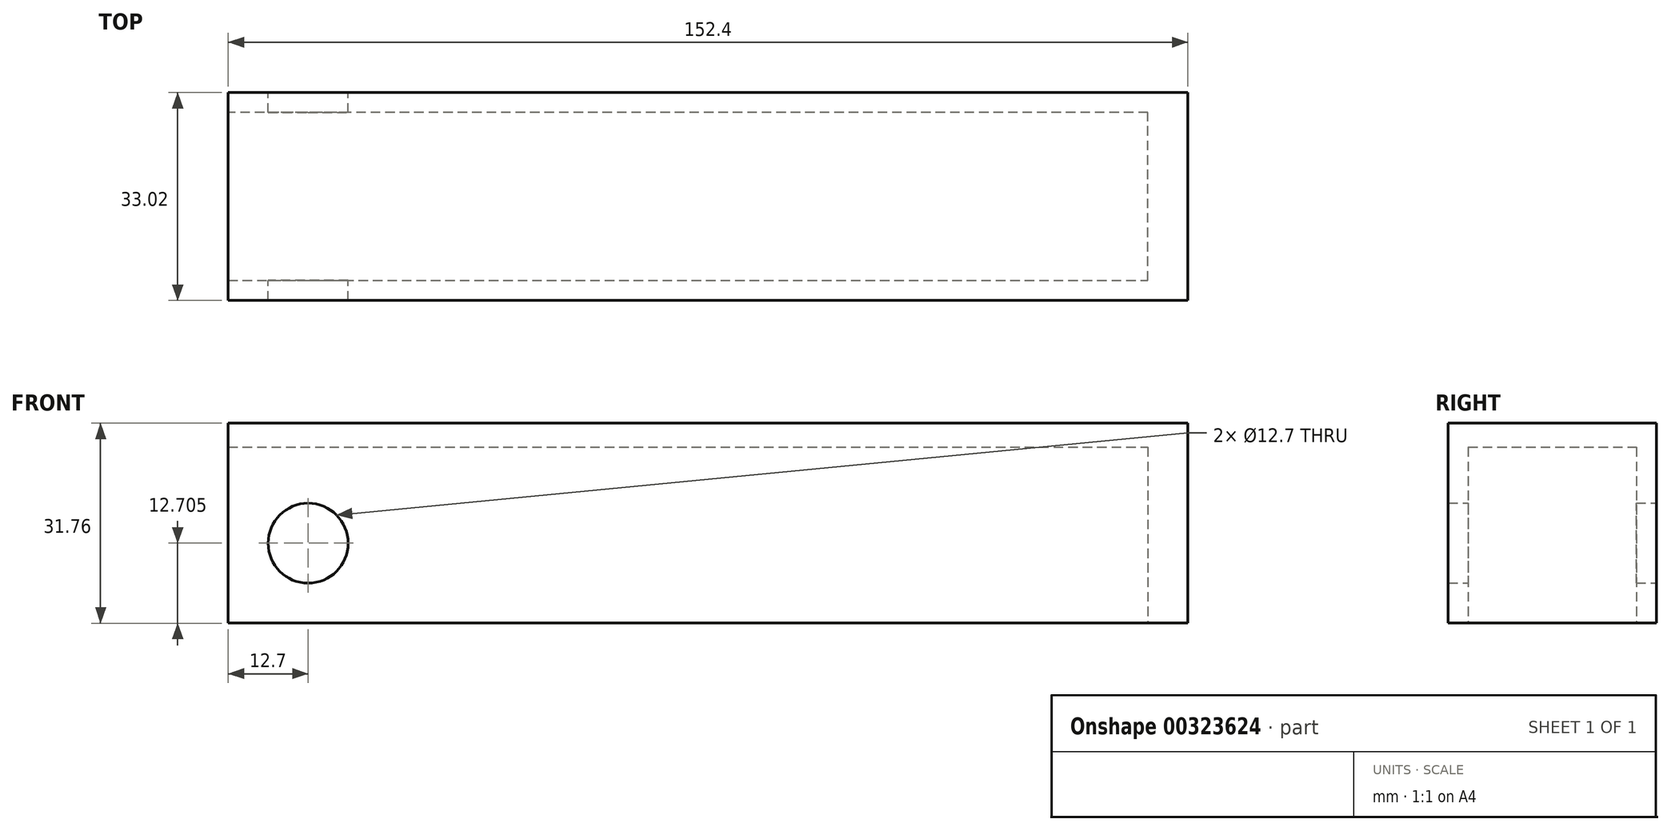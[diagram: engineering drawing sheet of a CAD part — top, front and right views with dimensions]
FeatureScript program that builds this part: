
annotation { "Feature Type Name" : "Feature", "Feature Type Description" : "" }
export const myFeature = defineFeature(function(context is Context, id is Id, definition is map)
    precondition{}
    {
        {
            var Q0;
            Q0=qCreatedBy(makeId("Front.planeOp"),FACE);
            var sketch = newSketch(context, id + "F0", { "sketchPlane" : qUnion([Q0])});
            skLineSegment(sketch, "E0.bottom", {"start": v(76.2, 15.88) * mm, "end": v(-76.2, 15.88) * mm});
            skLineSegment(sketch, "E0.top", {"start": v(76.2, -15.88) * mm, "end": v(-76.2, -15.88) * mm});
            skLineSegment(sketch, "E0.left", {"start": v(76.2, 15.88) * mm, "end": v(76.2, -15.88) * mm});
            skLineSegment(sketch, "E0.right", {"start": v(-76.2, 15.88) * mm, "end": v(-76.2, -15.88) * mm});
            skPoint(sketch, "E0.middle", {"position": v(0, 0) * mm});
            skCircle(sketch, "E1", {"center": v(-63.5, -3.17) * mm, "radius": 6.35 * mm});
            skSolve(sketch);
        }
        {
            var Q0;
            Q0=makeQuery(id+"F0.imprint","IMPRINT",FACE,{"disambiguationData":[TD([[makeQuery(id+"F0.imprint","IMPRINT",EDGE,{"derivedFrom":sQuery(id+"F0.wireOp",EDGE,"E0.bottom")}),1.0]])]});
            extrude(context, id + "F1", {"entities" : qUnion([Q0]), "depth" : 33.02 * mm});
        }
        {
            var Q0;
            Q0=makeQuery(id+"F1.opExtrude","SWEPT_FACE",FACE,{"disambiguationData":[OSD([sQuery(id+"F0.wireOp",EDGE,"E0.top")])]});
            var sketch = newSketch(context, id + "F2", { "sketchPlane" : qUnion([Q0])});
            skLineSegment(sketch, "E2", {"start": v(-76.2, 29.84) * mm, "end": v(69.85, 29.85) * mm});
            skLineSegment(sketch, "E3", {"start": v(69.85, 29.85) * mm, "end": v(69.85, 3.18) * mm});
            skLineSegment(sketch, "E4", {"start": v(69.85, 3.18) * mm, "end": v(-76.2, 3.18) * mm});
            skLineSegment(sketch, "E5", {"start": v(-76.2, 3.18) * mm, "end": v(-76.2, 29.84) * mm});
            skSolve(sketch);
        }
        {
            var Q0;
            Q0=makeQuery(id+"F2.imprint","IMPRINT",FACE,{"disambiguationData":[TD([[makeQuery(id+"F2.imprint","IMPRINT",EDGE,{"derivedFrom":sQuery(id+"F2.wireOp",EDGE,"E2")}),-1.0]])]});
            extrude(context, id + "F3", {"entities" : qUnion([Q0]), "operationType" : NewBodyOperationType.REMOVE, "oppositeDirection" : true, "depth" : 27.94 * mm});
        }
    });
